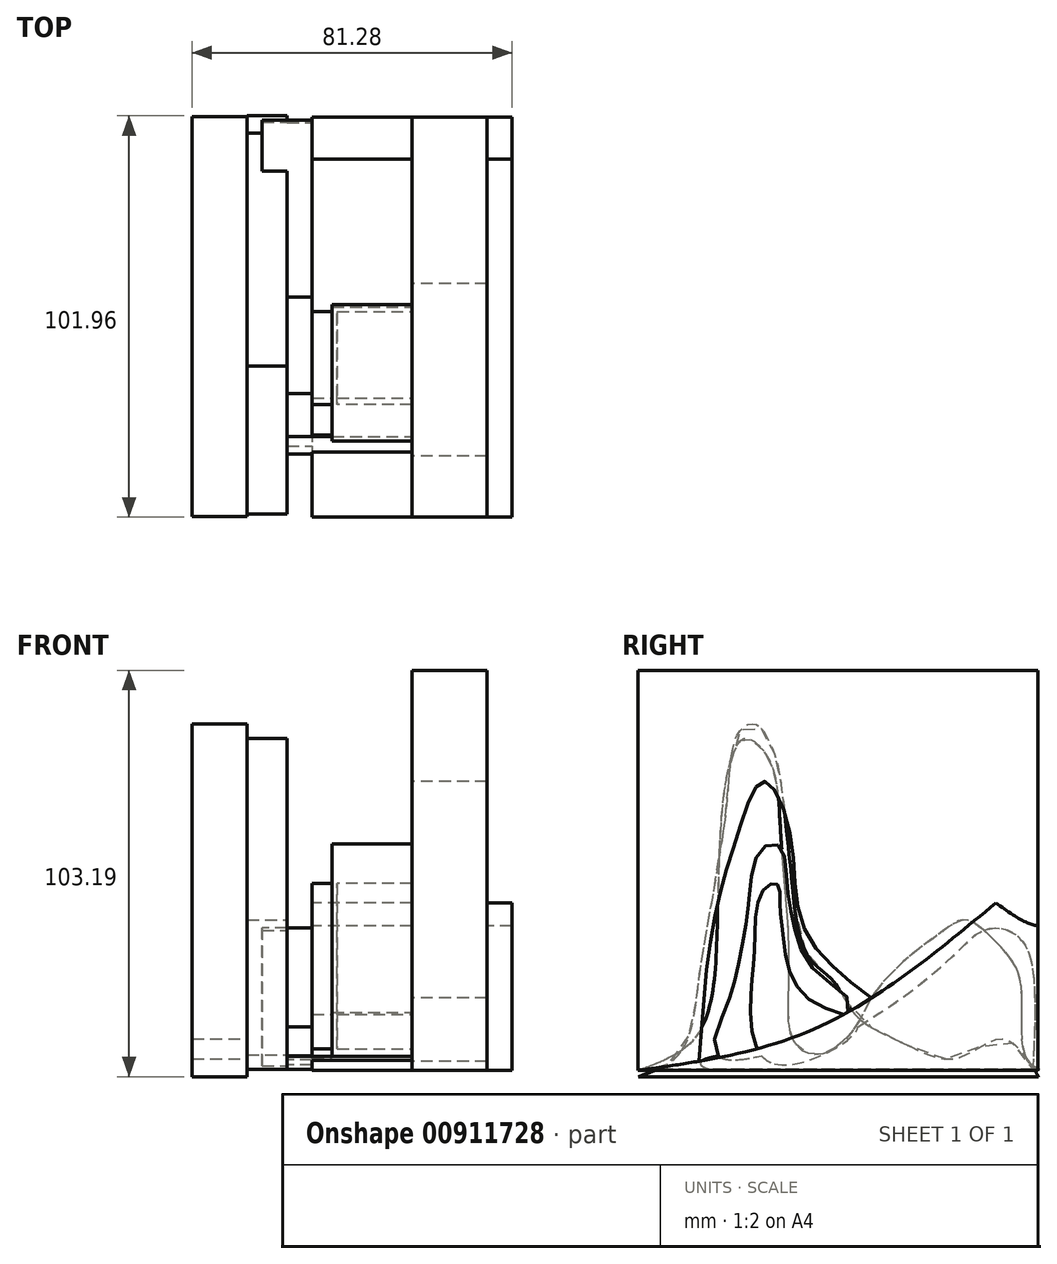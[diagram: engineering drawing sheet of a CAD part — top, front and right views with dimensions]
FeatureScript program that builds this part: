
annotation { "Feature Type Name" : "Feature", "Feature Type Description" : "" }
export const myFeature = defineFeature(function(context is Context, id is Id, definition is map)
    precondition{}
    {
        {
            var Q0;
            Q0=qCreatedBy(makeId("Right.planeOp"),FACE);
            var sketch = newSketch(context, id + "F0", { "sketchPlane" : qUnion([Q0])});
            skLineSegment(sketch, "E0", {"start": v(55.96, -101.6) * mm, "end": v(55.96, 0) * mm});
            skLineSegment(sketch, "E1", {"start": v(55.96, 0) * mm, "end": v(-45.64, 0) * mm});
            skLineSegment(sketch, "E2", {"start": v(-45.64, 0) * mm, "end": v(-45.64, -101.6) * mm});
            skLineSegment(sketch, "E3", {"start": v(-45.64, -101.6) * mm, "end": v(55.96, -101.6) * mm});
            skFitSpline(sketch, "E4", {"points": [v(-45.64, -101.6) * mm, v(0, -90.7) * mm, v(45.28, -59.03) * mm], "startDerivative": vector(97.11, 13.61) * mm, "endDerivative": vector(84.88, 70.75) * mm});
            skFitSpline(sketch, "E5", {"points": [v(-30.11, -99.42) * mm, v(-26.27, -62.97) * mm, v(-19.82, -40.19) * mm, v(-13.8, -28.15) * mm, v(-7.13, -40.62) * mm, v(-3.48, -65.34) * mm, v(13.71, -83.2) * mm], "startDerivative": vector(12.63, 182.22) * mm, "endDerivative": vector(120.66, -90.64) * mm});
            skFitSpline(sketch, "E6", {"points": [v(45.28, -59.03) * mm, v(52.3, -63.67) * mm, v(55.96, -64.9) * mm], "startDerivative": vector(12.58, -9.2) * mm, "endDerivative": vector(8.53, -2.1) * mm});
            skSolve(sketch);
        }
        {
            var Q0;
            {var subQ0=sQuery(id+"F0.wireOp",EDGE,"E3");Q0=makeQuery(id+"F0.imprint","IMPRINT",FACE,{"disambiguationData":[TD([[makeQuery(id+"F0.imprint","IMPRINT",EDGE,{"derivedFrom":subQ0}),1.0]])]});}
            extrude(context, id + "F1", {"entities" : qUnion([Q0]), "endBound" : BoundingType.SYMMETRIC, "depth" : 50.8 * mm, "offsetDistance" : 25.4 * mm});
        }
        {
            var Q0;
            {var subQ0=sQuery(id+"F0.wireOp",EDGE,"E5");var subQ1=sQuery(id+"F0.wireOp",EDGE,"E4");var subQ2=makeQuery(id+"F0.imprint","INTERSECT",VERTEX,{"disambiguationData":[OD(0.0)],"derivedFrom":[subQ1,subQ0]});Q0=makeQuery(id+"F0.imprint","IMPRINT",FACE,{"disambiguationData":[TD([[makeQuery(id+"F0.imprint","IMPRINT",EDGE,{"disambiguationData":[TD([[subQ2,1.0]])],"derivedFrom":subQ1}),1.0]])]});}
            extrude(context, id + "F2", {"entities" : qUnion([Q0]), "operationType" : NewBodyOperationType.ADD, "depth" : 19.05 * mm, "offsetDistance" : 25.4 * mm});
        }
        {
            var Q0;
            Q0=qCreatedBy(makeId("Right.planeOp"),FACE);
            var sketch = newSketch(context, id + "F3", { "sketchPlane" : qUnion([Q0])});
            skFitSpline(sketch, "E7", {"points": [v(8.1, -86.1) * mm, v(0, -77.04) * mm, v(-6.18, -64.11) * mm, v(-7.86, -53.03) * mm, v(-9.87, -44.47) * mm, v(-14.57, -45.64) * mm, v(-17.26, -56.05) * mm, v(-18.1, -63.44) * mm, v(-20.45, -76.37) * mm, v(-23.64, -86.44) * mm, v(-24.65, -98.36) * mm, v(8.1, -86.1) * mm]});
            skFitSpline(sketch, "E8", {"points": [v(10.22, -90.49) * mm, v(-2.35, -83.43) * mm, v(-8.7, -68.04) * mm, v(-9.55, -59.14) * mm, v(-10.4, -54.2) * mm, v(-14.07, -56.18) * mm, v(-16.04, -70.3) * mm, v(-17.03, -84.41) * mm, v(-10.96, -99.94) * mm, v(10.22, -90.49) * mm]});
            skFitSpline(sketch, "E9", {"points": [v(10.22, -90.49) * mm, v(24.06, -81.24) * mm, v(36.32, -70.66) * mm, v(41.52, -66.3) * mm, v(47.4, -65.63) * mm, v(52.44, -69.32) * mm, v(54.79, -77.2) * mm, v(55.12, -90.49) * mm, v(54.62, -101.39) * mm], "startDerivative": vector(86.2, 53.64) * mm, "endDerivative": vector(-4.65, -80.5) * mm});
            skLineSegment(sketch, "E10", {"start": v(54.62, -101.39) * mm, "end": v(-10.83, -101.39) * mm});
            skLineSegment(sketch, "E11", {"start": v(-10.83, -101.39) * mm, "end": v(-27.6, -101.39) * mm});
            skFitSpline(sketch, "E12", {"points": [v(-27.6, -101.39) * mm, v(-29.49, -100.38) * mm, v(-29.4, -99.29) * mm, v(-25.24, -97.98) * mm], "startDerivative": vector(-7.4, 2.57) * mm, "endDerivative": vector(11.74, 2.12) * mm});
            skLineSegment(sketch, "E13", {"start": v(-10.96, -99.94) * mm, "end": v(-10.83, -101.39) * mm});
            skSolve(sketch);
        }
        {
            var Q0;
            Q0=makeQuery(id+"F3.imprint","IMPRINT",FACE,{"disambiguationData":[TD([[makeQuery(id+"F3.imprint","IMPRINT",EDGE,{"derivedFrom":sQuery(id+"F3.wireOp",EDGE,"E7")}),1.0]])]});
            extrude(context, id + "F4", {"entities" : qUnion([Q0]), "operationType" : NewBodyOperationType.ADD, "oppositeDirection" : true, "depth" : 10.16 * mm, "offsetDistance" : 25.4 * mm});
        }
        {
            var Q0;
            {var subQ0=sQuery(id+"F3.wireOp",EDGE,"E8");var subQ1=sQuery(id+"F3.wireOp",EDGE,"E7");var subQ2=makeQuery(id+"F3.imprint","INTERSECT",VERTEX,{"disambiguationData":[OD(0.0)],"derivedFrom":[subQ1,subQ0]});Q0=makeQuery(id+"F3.imprint","IMPRINT",FACE,{"disambiguationData":[TD([[makeQuery(id+"F3.imprint","IMPRINT",EDGE,{"disambiguationData":[TD([[subQ2,-1.0]])],"derivedFrom":subQ1}),1.0]])]});}
            extrude(context, id + "F5", {"entities" : qUnion([Q0]), "operationType" : NewBodyOperationType.ADD, "oppositeDirection" : true, "depth" : 20.32 * mm, "offsetDistance" : 25.4 * mm});
        }
        {
            var Q0;
            Q0=makeQuery(id+"F3.imprint","IMPRINT",FACE,{"disambiguationData":[TD([[makeQuery(id+"F3.imprint","IMPRINT",EDGE,{"derivedFrom":sQuery(id+"F3.wireOp",EDGE,"E11")}),-1.0]])]});
            var Q1;
            {var subQ0=sQuery(id+"F3.wireOp",EDGE,"E9");Q1=makeQuery(id+"F3.imprint","IMPRINT",FACE,{"disambiguationData":[TD([[makeQuery(id+"F3.imprint","IMPRINT",EDGE,{"derivedFrom":subQ0}),-1.0]])]});}
            extrude(context, id + "F6", {"entities" : qUnion([Q0, Q1]), "operationType" : NewBodyOperationType.ADD, "oppositeDirection" : true, "depth" : 38.1 * mm, "offsetDistance" : 25.4 * mm});
        }
        {
            var Q0;
            {var subQ0=sQuery(id+"F3.wireOp",EDGE,"E8");var subQ1=sQuery(id+"F3.wireOp",EDGE,"E7");var subQ2=makeQuery(id+"F3.imprint","INTERSECT",VERTEX,{"disambiguationData":[OD(0.0)],"derivedFrom":[subQ1,subQ0]});Q0=makeQuery(id+"F3.imprint","IMPRINT",FACE,{"disambiguationData":[TD([[makeQuery(id+"F3.imprint","IMPRINT",EDGE,{"disambiguationData":[TD([[subQ2,1.0]])],"derivedFrom":subQ1}),1.0]])]});}
            extrude(context, id + "F7", {"entities" : qUnion([Q0]), "operationType" : NewBodyOperationType.ADD, "oppositeDirection" : true, "depth" : 25.4 * mm, "offsetDistance" : 25.4 * mm, "hasSecondDirection" : true, "secondDirectionOppositeDirection" : true, "secondDirectionDepth" : 19.05 * mm});
        }
        {
            var Q0;
            Q0=qCreatedBy(makeId("Right.planeOp"),FACE);
            var sketch = newSketch(context, id + "F8", { "sketchPlane" : qUnion([Q0])});
            skLineSegment(sketch, "E14", {"start": v(56.32, -101.4) * mm, "end": v(-44.87, -101.4) * mm});
            skFitSpline(sketch, "E15", {"points": [v(56.32, -101.4) * mm, v(53.55, -99.36) * mm, v(51.9, -93.08) * mm, v(51.7, -79.79) * mm, v(49.12, -73.32) * mm, v(43.95, -67.6) * mm, v(37.49, -63.35) * mm, v(32.5, -65.75) * mm, v(25.67, -70.74) * mm, v(20.68, -74.98) * mm, v(14.04, -82.56) * mm, v(8.87, -91.6) * mm, v(0, -97.7) * mm, v(-6.1, -94.19) * mm, v(-7.38, -83.1) * mm, v(-7.38, -67.23) * mm, v(-8.12, -56.89) * mm, v(-9.6, -37.87) * mm, v(-12.22, -22.69) * mm, v(-18.68, -17.33) * mm, v(-23.85, -31.18) * mm, v(-25.51, -65.34) * mm, v(-30.5, -92.49) * mm, v(-44.87, -101.4) * mm], "startDerivative": vector(-126.76, 66.78) * mm, "endDerivative": vector(-312.12, -116.58) * mm});
            skSolve(sketch);
        }
        {
            var Q0;
            Q0=makeQuery(id+"F8.imprint","IMPRINT",FACE,{"disambiguationData":[TD([[makeQuery(id+"F8.imprint","IMPRINT",EDGE,{"derivedFrom":sQuery(id+"F8.wireOp",EDGE,"E14")}),-1.0]])]});
            extrude(context, id + "F9", {"entities" : qUnion([Q0]), "operationType" : NewBodyOperationType.ADD, "oppositeDirection" : true, "depth" : 41.9 * mm, "offsetDistance" : 25.4 * mm, "hasSecondDirection" : true, "secondDirectionOppositeDirection" : true, "secondDirectionDepth" : 31.75 * mm});
        }
        {
            var Q0;
            Q0=qCreatedBy(makeId("Right.planeOp"),FACE);
            var sketch = newSketch(context, id + "F10", { "sketchPlane" : qUnion([Q0])});
            skLineSegment(sketch, "E16", {"start": v(56.13, -103.2) * mm, "end": v(-45.5, -103.2) * mm});
            skFitSpline(sketch, "E17", {"points": [v(-45.5, -103.2) * mm, v(-35.84, -98.14) * mm, v(-31.64, -89.1) * mm, v(-29.81, -75.93) * mm, v(-23.05, -34.24) * mm, v(-20.02, -15.69) * mm, v(-15.66, -13.71) * mm, v(-12, -18.78) * mm, v(-10.06, -24.45) * mm, v(-7.88, -41.12) * mm, v(-6.52, -53.7) * mm, v(-2.7, -72.2) * mm, v(3.87, -78.75) * mm, v(9.81, -87.72) * mm, v(21.2, -94.43) * mm, v(35.29, -98.5) * mm, v(46.72, -93.55) * mm, v(56.13, -103.2) * mm], "startDerivative": vector(200.97, 71.67) * mm, "endDerivative": vector(147.4, -237.3) * mm});
            skSolve(sketch);
        }
        {
            var Q0;
            Q0=makeQuery(id+"F10.imprint","IMPRINT",FACE,{"disambiguationData":[TD([[makeQuery(id+"F10.imprint","IMPRINT",EDGE,{"derivedFrom":sQuery(id+"F10.wireOp",EDGE,"E16")}),-1.0]])]});
            extrude(context, id + "F11", {"entities" : qUnion([Q0]), "operationType" : NewBodyOperationType.ADD, "oppositeDirection" : true, "depth" : 55.88 * mm, "offsetDistance" : 25.4 * mm, "hasSecondDirection" : true, "secondDirectionOppositeDirection" : true, "secondDirectionDepth" : 41.9 * mm});
        }
    });
